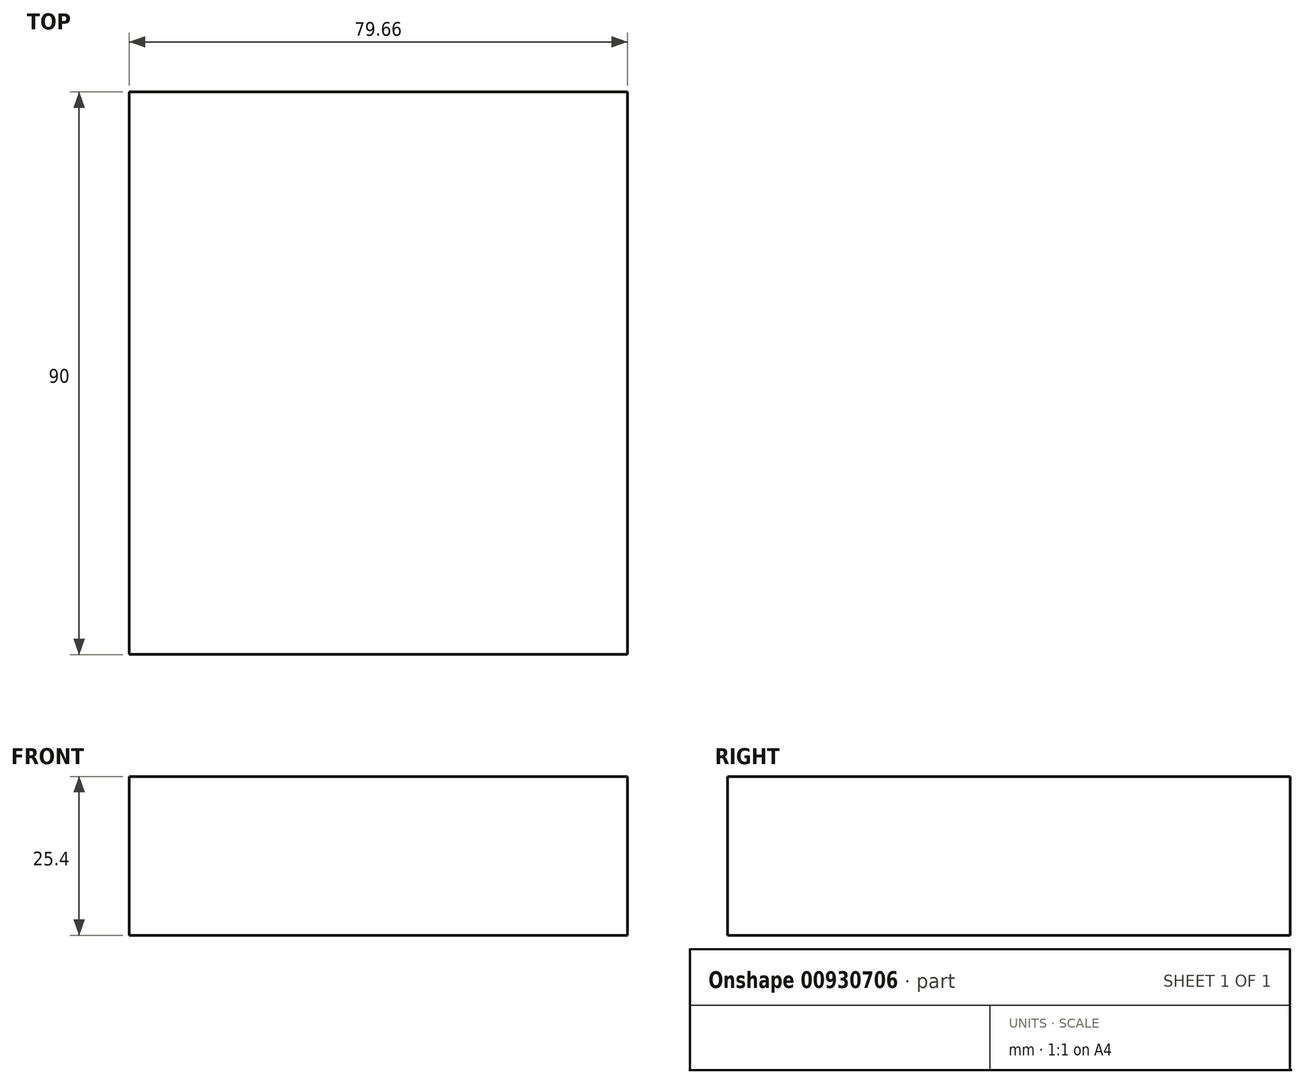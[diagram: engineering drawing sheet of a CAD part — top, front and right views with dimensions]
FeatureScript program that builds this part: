
annotation { "Feature Type Name" : "Feature", "Feature Type Description" : "" }
export const myFeature = defineFeature(function(context is Context, id is Id, definition is map)
    precondition{}
    {
        {
            var Q0;
            Q0=qCreatedBy(makeId("Top.planeOp"),FACE);
            var sketch = newSketch(context, id + "F0", { "sketchPlane" : qUnion([Q0])});
            skLineSegment(sketch, "E0.bottom", {"start": v(39.83, 45) * mm, "end": v(-39.83, 45) * mm});
            skLineSegment(sketch, "E0.top", {"start": v(39.83, -45) * mm, "end": v(-39.83, -45) * mm});
            skLineSegment(sketch, "E0.left", {"start": v(39.83, 45) * mm, "end": v(39.83, -45) * mm});
            skLineSegment(sketch, "E0.right", {"start": v(-39.83, 45) * mm, "end": v(-39.83, -45) * mm});
            skLineSegment(sketch, "E1", {"start": v(39.83, 45) * mm, "end": v(-39.83, -45) * mm, "construction": true});
            skLineSegment(sketch, "E2", {"start": v(39.83, -45) * mm, "end": v(-39.83, 45) * mm, "construction": true});
            skSolve(sketch);
        }
        {
            var Q0;
            Q0=makeQuery(id+"F0.imprint","IMPRINT",FACE,{"disambiguationData":[TD([[makeQuery(id+"F0.imprint","IMPRINT",EDGE,{"derivedFrom":sQuery(id+"F0.wireOp",EDGE,"E0.bottom")}),1.0]])]});
            extrude(context, id + "F1", {"entities" : qUnion([Q0]), "depth" : 25.4 * mm, "offsetDistance" : 25.4 * mm});
        }
    });
